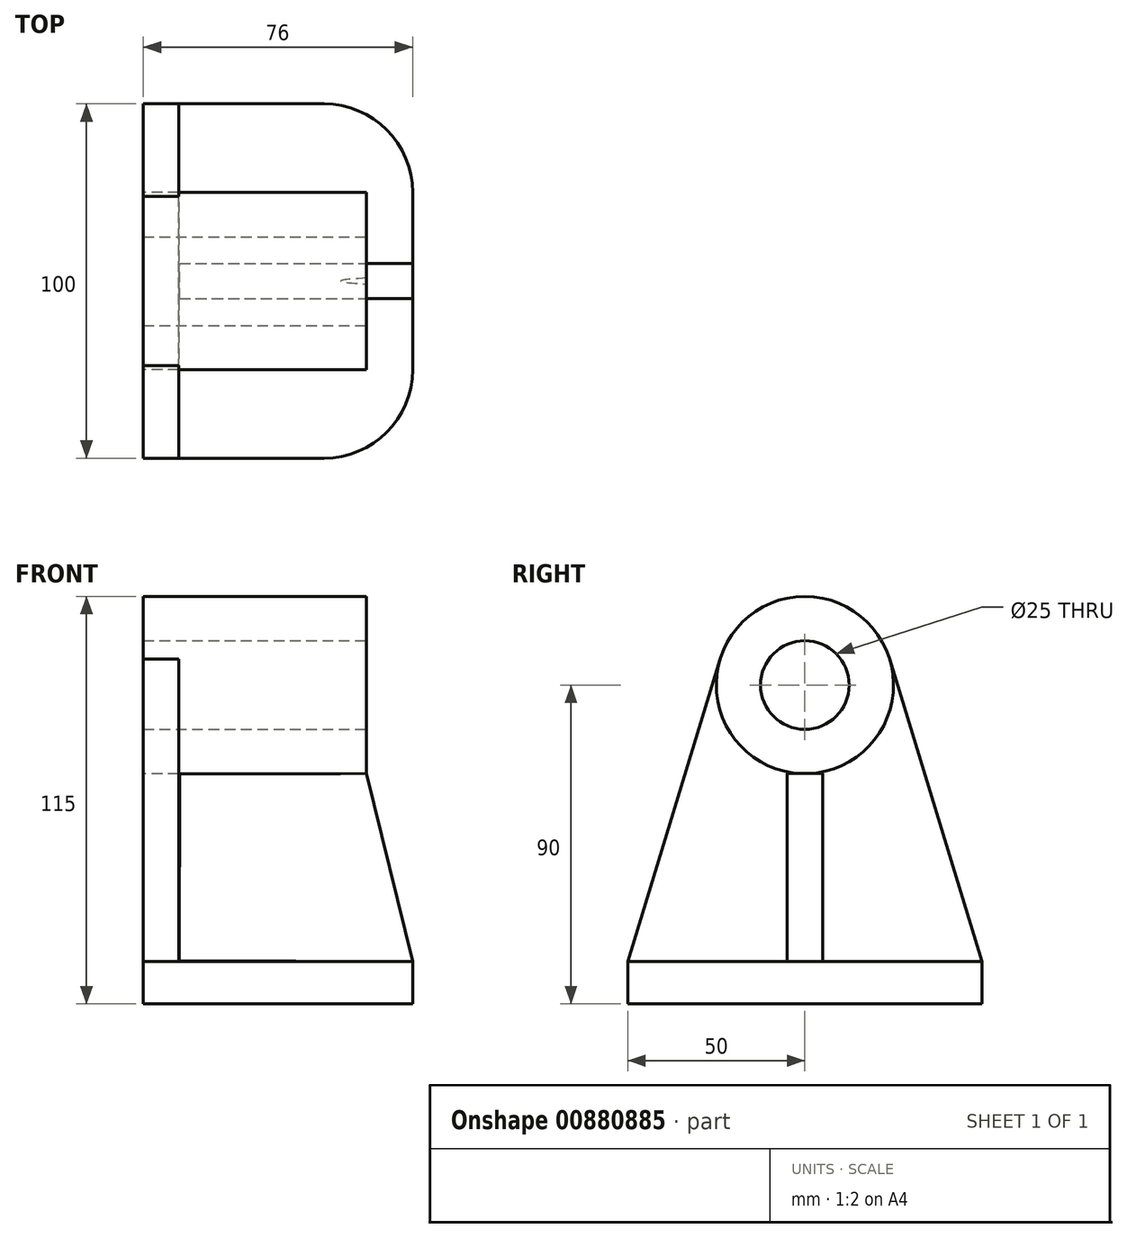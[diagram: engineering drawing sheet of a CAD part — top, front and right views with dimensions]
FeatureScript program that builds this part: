
annotation { "Feature Type Name" : "Feature", "Feature Type Description" : "" }
export const myFeature = defineFeature(function(context is Context, id is Id, definition is map)
    precondition{}
    {
        {
            var Q0;
            Q0=qCreatedBy(makeId("Top.planeOp"),FACE);
            var sketch = newSketch(context, id + "F0", { "sketchPlane" : qUnion([Q0])});
            skLineSegment(sketch, "E0.bottom", {"start": v(-38, 50) * mm, "end": v(38, 50) * mm});
            skLineSegment(sketch, "E0.top", {"start": v(-38, -50) * mm, "end": v(38, -50) * mm});
            skLineSegment(sketch, "E0.left", {"start": v(-38, 50) * mm, "end": v(-38, -50) * mm});
            skLineSegment(sketch, "E0.right", {"start": v(38, 50) * mm, "end": v(38, -50) * mm});
            skSolve(sketch);
        }
        {
            var Q0;
            Q0 = qSketchRegion(id + "F0", true);
            extrude(context, id + "F1", {"entities" : qUnion([Q0]), "depth" : 12 * mm, "offsetDistance" : 25 * mm});
        }
        {
            var Q0;
            Q0=makeQuery(id+"F1.opExtrude","SWEPT_EDGE",EDGE,{"disambiguationData":[OSD([sQuery(id+"F0.wireOp",EDGE,"E0.top"),sQuery(id+"F0.wireOp",EDGE,"E0.right")])]});
            var Q1;
            Q1=makeQuery(id+"F1.opExtrude","SWEPT_EDGE",EDGE,{"disambiguationData":[OSD([sQuery(id+"F0.wireOp",EDGE,"E0.bottom"),sQuery(id+"F0.wireOp",EDGE,"E0.right")])]});
            fillet(context, id + "F2", {"entities" : qUnion([Q0, Q1]), "radius" : 25 * mm, "tangentPropagation" : true, "allowEdgeOverflow" : false});
        }
        {
            var Q0;
            Q0=qCreatedBy(makeId("Right.planeOp"),FACE);
            var sketch = newSketch(context, id + "F3", { "sketchPlane" : qUnion([Q0])});
            skCircle(sketch, "E1", {"center": v(0, 90) * mm, "radius": 25 * mm});
            skSolve(sketch);
        }
        {
            var Q0;
            Q0 = qSketchRegion(id + "F3", true);
            extrude(context, id + "F4", {"entities" : qUnion([Q0]), "depth" : 25 * mm, "offsetDistance" : 25 * mm});
        }
        {
            var Q0;
            Q0=makeQuery(id+"F4.opExtrude","CAP_FACE",FACE,{"disambiguationData":[OSD([sQuery(id+"F3.wireOp",EDGE,"E1")])],"isStart":false});
            var sketch = newSketch(context, id + "F5", { "sketchPlane" : qUnion([Q0])});
            skLineSegment(sketch, "E2", {"start": v(0, 0) * mm, "end": v(0, 126.47) * mm, "construction": true});
            skCircle(sketch, "E3", {"center": v(0, 90) * mm, "radius": 12.5 * mm});
            skSolve(sketch);
        }
        {
            var Q0;
            Q0 = qSketchRegion(id + "F5", true);
            extrude(context, id + "F6", {"entities" : qUnion([Q0]), "operationType" : NewBodyOperationType.REMOVE, "depth" : 63 * mm, "offsetDistance" : 25 * mm});
        }
        {
            var Q0;
            Q0=makeQuery(id+"F4.opExtrude","CAP_FACE",FACE,{"disambiguationData":[OSD([sQuery(id+"F3.wireOp",EDGE,"E1")])],"isStart":false});
            extrude(context, id + "F7", {"entities" : qUnion([Q0]), "operationType" : NewBodyOperationType.ADD, "oppositeDirection" : true, "depth" : 63 * mm, "offsetDistance" : 25 * mm});
        }
        {
            var Q0;
            Q0=makeQuery(id+"F4.opExtrude","CAP_FACE",FACE,{"disambiguationData":[OSD([sQuery(id+"F3.wireOp",EDGE,"E1")])],"isStart":false});
            var sketch = newSketch(context, id + "F8", { "sketchPlane" : qUnion([Q0])});
            skCircle(sketch, "E4", {"center": v(0, 90) * mm, "radius": 12.5 * mm});
            skSolve(sketch);
        }
        {
            var Q0;
            Q0 = qSketchRegion(id + "F8", true);
            extrude(context, id + "F9", {"entities" : qUnion([Q0]), "operationType" : NewBodyOperationType.REMOVE, "endBound" : BoundingType.THROUGH_ALL, "oppositeDirection" : true, "depth" : 25 * mm, "offsetDistance" : 25 * mm});
        }
        {
            var Q0;
            Q0=makeQuery(id+"F7.opExtrude","CAP_FACE",FACE,{"disambiguationData":[OSD([sQuery(id+"F3.wireOp",EDGE,"E1")])],"isStart":false});
            var sketch = newSketch(context, id + "F10", { "sketchPlane" : qUnion([Q0])});
            skLineSegment(sketch, "E5", {"start": v(-23.9, 97.31) * mm, "end": v(-50, 12) * mm});
            skLineSegment(sketch, "E6", {"start": v(-50, 12) * mm, "end": v(50, 12) * mm});
            skLineSegment(sketch, "E7", {"start": v(50, 12) * mm, "end": v(23.9, 97.31) * mm});
            skSolve(sketch);
        }
        {
            var Q0;
            {var subQ0=sQuery(id+"F10.wireOp",EDGE,"E5");Q0=makeQuery(id+"F10.imprint","IMPRINT",FACE,{"disambiguationData":[TD([[makeQuery(id+"F10.imprint","IMPRINT",EDGE,{"derivedFrom":subQ0}),1.0]])]});}
            extrude(context, id + "F11", {"entities" : qUnion([Q0]), "oppositeDirection" : true, "depth" : 10 * mm, "offsetDistance" : 25 * mm});
        }
        {
            var Q0;
            Q0=qCreatedBy(makeId("Front.planeOp"),FACE);
            var sketch = newSketch(context, id + "F12", { "sketchPlane" : qUnion([Q0])});
            skLineSegment(sketch, "E8", {"start": v(25, 65.01) * mm, "end": v(38, 12) * mm});
            skLineSegment(sketch, "E9", {"start": v(-27.86, 12.24) * mm, "end": v(38, 12) * mm});
            skLineSegment(sketch, "E10", {"start": v(-27.86, 12.24) * mm, "end": v(-27.67, 64.91) * mm});
            skLineSegment(sketch, "E11", {"start": v(-27.67, 64.91) * mm, "end": v(25, 65.01) * mm});
            skSolve(sketch);
        }
        {
            var Q0;
            Q0 = qSketchRegion(id + "F12", true);
            extrude(context, id + "F13", {"entities" : qUnion([Q0]), "operationType" : NewBodyOperationType.ADD, "endBound" : BoundingType.SYMMETRIC, "depth" : 10 * mm, "offsetDistance" : 25 * mm});
        }
        {
            var Q0;
            Q0=qCreatedBy(makeId("Top.planeOp"),FACE);
            cPlane(context, id + "F15", {"entities" : qUnion([Q0]), "cplaneType" : CPlaneType.OFFSET, "offset" : (90 + 48) * mm, "width" : 150 * mm, "height" : 150 * mm});
        }
    });
